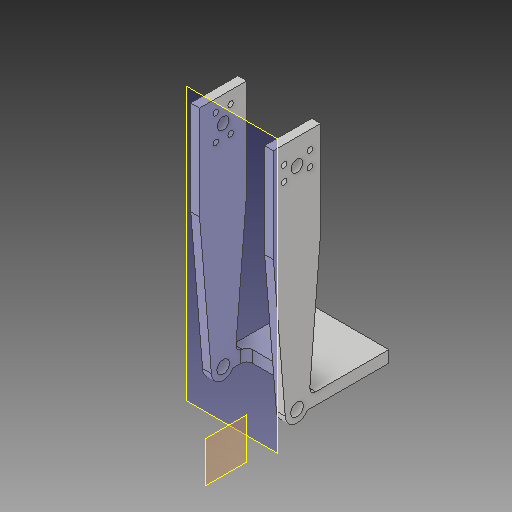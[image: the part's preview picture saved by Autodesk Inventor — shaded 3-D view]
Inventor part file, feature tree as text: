
AUTODESK INVENTOR PART (.ipt)
format: ipt  version: 2019 (Build 230136000, 136)  size: 261,120 bytes
history: native  units: in
note: dims shown in document units (in); Inventor stores cm internally (conversion verified against a paired STEP export)
features: sketch x9, projected_geometry x9, hole x5, extrude x4, plane x3, fillet x2, mirror x1
ambient origin geometry x8: Origin, YZ Plane, XZ Plane, XY Plane, X Axis, Y Axis, Z Axis, Center Point
bodies: Solid1 (feature_tree)
feature tree (33):
  sketch  "Sketch1"  dims[d0=5.0in d1=1.0in]
  plane  "Work Plane1"
  extrude  "Extrusion2"  Depth=1.0in
  plane  "Work Plane2"
  extrude  "Extrusion3"  Depth=1.0in
  hole  "Hole2"  [1 undecoded]
  extrude  "Extrusion4"  Depth=1.753in
  extrude  "Extrusion5"  Depth=1.753in
  fillet  "Fillet1"  Radius=2.0in
  fillet  "Fillet2"  Radius=1.753in
  hole  "Hole3"  [1 undecoded]
  hole  "Hole4"  [1 undecoded]
  hole  "Hole5"  [1 undecoded]
  hole  "Hole6"  [1 undecoded]
  plane  "Work Plane3"
  mirror  "Mirror1"
  sketch  "Sketch2"  dims[d5=1.0in d6=0.5in]
  projected_geometry  "Projected Loop1"
  sketch  "Sketch4"  dims[d7=0.5in d8=0.0in]
  projected_geometry  "Projected Loop3"
  sketch  "Sketch5"  dims[d9=1.753in d10=0.0in d18=0.5in]
  projected_geometry  "Projected Loop4"
  sketch  "Sketch8"  dims[d19=0.25in d20=2.0in d21=2.0in d22=1.753in d23=0.0in]
  projected_geometry  "Projected Loop9"
  projected_geometry  "Projected Loop10"
  sketch  "Sketch9"  dims[d24=0.27in d25=0.75in d26=0.375in d27=0.25in d28=0.5635in d29=1.0in d30=0.8108in d31=1.75in]
  projected_geometry  "Projected Loop11"
  sketch  "Sketch10"  dims[d32=0.25in d35=5.0in]
  projected_geometry  "Projected Loop12"
  sketch  "Sketch11"  dims[d36=4.875in d37=1.753in d38=0.0in]
  projected_geometry  "Projected Loop13"
  sketch  "Sketch12"  dims[d41=1.753in d42=5.375in d43=1.378in d44=0.1875in d45=5.875in d46=1.0in d47=0.0in d48=0.125in d49=0.125in d50=0.6299in d51=1.0in d52=0.5in d55=0.117in d56=0.75in d57=0.375in d58=0.25in d59=0.5635in d60=1.0in d61=0.8108in d62=0.6299in d63=1.0in d64=0.5in d67=0.117in d68=0.75in d69=0.375in d70=0.25in d71=0.5635in d72=1.0in d73=0.8108in d74=0.32in d75=1.753in d77=0.5in d78=0.75in d79=0.375in d80=0.25in d81=0.5635in d82=0.125in d83=0.0in d84=1.0in d85=0.5in d86=0.315in d87=0.1575in d88=0.25in d89=0.75in d90=0.375in d91=0.25in d92=0.5635in d93=1.0in d94=0.8108in d95=0.27in d96=0.1975in d97=0.375in d98=0.315in d99=0.1575in d100=0.53in d101=0.315in d102=0.1575in d103=0.53in]
  projected_geometry  "Projected Loop14"
note: 5 required parameter values undecoded (feature->parameter linkage not recoverable at this tier; creation-order binding heuristic only, values carry confidence <= 0.55)
